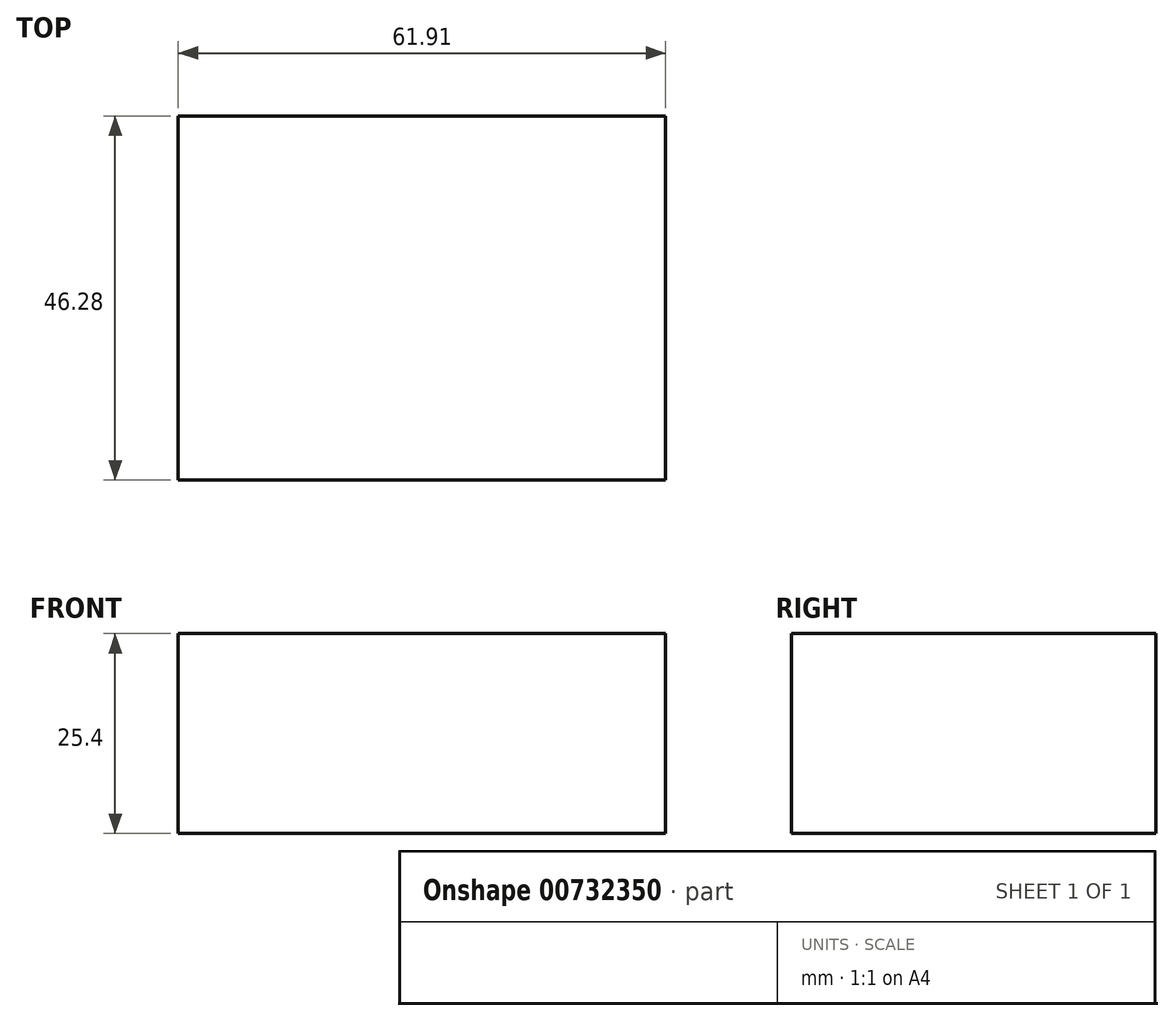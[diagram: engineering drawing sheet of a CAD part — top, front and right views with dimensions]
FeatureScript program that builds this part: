
annotation { "Feature Type Name" : "Feature", "Feature Type Description" : "" }
export const myFeature = defineFeature(function(context is Context, id is Id, definition is map)
    precondition{}
    {
        {
            var Q0;
            Q0=qCreatedBy(makeId("Top.planeOp"),FACE);
            var sketch = newSketch(context, id + "F0", { "sketchPlane" : qUnion([Q0])});
            skLineSegment(sketch, "E0.bottom", {"start": v(-36.65, -14.93) * mm, "end": v(25.26, -14.93) * mm});
            skLineSegment(sketch, "E0.top", {"start": v(-36.65, 31.35) * mm, "end": v(25.26, 31.35) * mm});
            skLineSegment(sketch, "E0.left", {"start": v(-36.65, -14.93) * mm, "end": v(-36.65, 31.35) * mm});
            skLineSegment(sketch, "E0.right", {"start": v(25.26, -14.93) * mm, "end": v(25.26, 31.35) * mm});
            skSolve(sketch);
        }
        {
            var Q0;
            Q0 = qSketchRegion(id + "F0", true);
            extrude(context, id + "F1", {"entities" : qUnion([Q0]), "depth" : 25.4 * mm, "offsetDistance" : 25.4 * mm});
        }
    });
